# Revit family: Sink-Wall_Mount-KOHLER-Brenham-K-1997
name_source: partatom
category: Plumbing Fixtures
revit_build: Autodesk Revit 2015 (Build: 20140606_1530(x64)
units: mm (PartAtom-declared; Revit-internal decimal feet)

## types (35) — shared parameters
ADA Compliant = Yes
Assembly Code = D2010400
CW Connection = No
Cold Water Inlet = Cold Water Inlet
Date Modified = 08/20/2018
Default Elevation = 34"
Drain Included = No
HW Connection = No
Height = 6 9/16"
Hot Water Inlet = Hot Water Inlet
Length = 21 15/16"
Manufacturer = KOHLER Co.
MasterFormat 1995 = 15410
MasterFormat 2004 = 22.41.16
Material = Vitreous china
Product Documentation Link = http://www.us.kohler.com
Product Name = Brenham
Product Page URL = http://www.us.kohler.com
URL = https://www.us.kohler.com
Vent Connection = No
Waste Connection = Yes
Waste Water Outlet = Waste Water Outlet
Width = 19 3/4"

## per-type parameters (varying)
| type | 1L_SS1L | 1NL_SS1NL | 1NR_SS1NR | 1N_SS1N | 1R_SS1R | 1_SS1 | 4N_SS4N | 4_SS4 | 8N_SS8N | 8_SS8 | Description | Environmental Product Declaration | Finish | Model | Type |
| Antimicrobial Finish, 4" Faucet Holes, 0-White | No | No | No | No | No | No | No | Yes | No | No | Wall-mounted or concealed carrier arm mounted commercial bathroom sink with 4 Inch centerset faucet holes, antimicrobial finish |  | Kohler-Vitreous_China-0-White | K-1997-SS4-0 | 1 |
| Antimicrobial Finish, No Overflow, 4" Faucet Holes,0-White | No | No | No | No | No | No | Yes | No | No | No | Wall-mounted or concealed carrier arm mounted commercial bathroom sink with 4 Inch centerset faucet holes and no overflow, antimicrobial finish |  | Kohler-Vitreous_China-0-White | K-1997-SS4N-0 | 2 |
| Antimicrobial Finish, 8" Faucet Holes,0-White | No | No | No | No | No | No | No | No | No | Yes | Wall-mounted or concealed carrier arm mounted commercial bathroom sink with widespread faucet holes, antimicrobial finish |  | Kohler-Vitreous_China-0-White | K-1997-SS8-0 | 3 |
| Antimicrobial Finish, No Overflow, 8" Faucet Holes, 0-White | No | No | No | No | No | No | No | No | Yes | No | Wall-mounted or concealed carrier arm mounted commercial bathroom sink with widespread faucet holes and no overflow, antimicrobial finish |  | Kohler-Vitreous_China-0-White | K-1997-SS8N-0 | 4 |
| Antimicrobial Finish, No Overflow, Left Soap Dispenser, 1 Faucet Hole, 0-White | No | Yes | No | No | No | No | No | No | No | No | Wall-mounted or concealed carrier arm mounted commercial bathroom sink with single faucet hole, no overflow and left-hand soap dispenser hole, antimicrobial finish |  | Kohler-Vitreous_China-0-White | K-1997-SS1NL-0 | 5 |
| Antimicrobial Finish, Right Soap Dispenser, 1 Faucet Hole, 0-White | No | No | No | No | Yes | No | No | No | No | No | Wall-mounted or concealed carrier arm mounted commercial bathroom sink with single faucet hole and right-hand soap dispenser hole, antimicrobial finish |  | Kohler-Vitreous_China-0-White | K-1997-SS1R-0 | 6 |
| Antimicrobial Finish, No Overflow, 1 Faucet Hole, 0-White | No | No | No | Yes | No | No | No | No | No | No | Wall-mounted or concealed carrier arm mounted commercial bathroom sink with single faucet hole and no overflow, antimicrobial finish |  | Kohler-Vitreous_China-0-White | K-1997-SS1N-0 | 7 |
| Antimicrobial Finish, No Overflow, Right Soap Dispenser, 1 Faucet Hole, 0-White | No | No | Yes | No | No | No | No | No | No | No | Wall-mounted or concealed carrier arm mounted commercial bathroom sink with single faucet hole, no overflow and right-hand soap dispenser hole, antimicrobial finish |  | Kohler-Vitreous_China-0-White | K-1997-SS1NR-0 | 8 |
| Antimicrobial Finish, Left Soap Dispenser, 1 Faucet Hole, 0-White | Yes | No | No | No | No | No | No | No | No | No | Wall-mounted or concealed carrier arm mounted commercial bathroom sink with single faucet hole and left-hand soap dispenser hole, antimicrobial finish |  | Kohler-Vitreous_China-0-White | K-1997-SS1L-0 | 9 |
| Antimicrobial Finish, 1 Faucet Hole, 0-White | No | No | No | No | No | Yes | No | No | No | No | Wall-mounted or concealed carrier arm mounted commercial bathroom sink with single faucet hole, antimicrobial finish |  | Kohler-Vitreous_China-0-White | K-1997-SS1-0 | 10 |
| 4" Faucet Holes, 0-White | No | No | No | No | No | No | No | Yes | No | No | Wall-mounted or concealed carrier arm mounted commercial bathroom sink with 4 Inch center set faucet holes | https://www.us.kohler.com | Kohler-Vitreous_China-0-White | K-1997-4-0 | 11 |
| 4" Faucet Holes, 96-Biscuit | No | No | No | No | No | No | No | Yes | No | No | Wall-mounted or concealed carrier arm mounted commercial bathroom sink with 4 Inch center set faucet holes | https://www.us.kohler.com | Kohler-Vitreous_China-96-Biscuit | K-1997-4-96 | 12 |
| 4" Faucet Holes, 47-Almond | No | No | No | No | No | No | No | Yes | No | No | Wall-mounted or concealed carrier arm mounted commercial bathroom sink with 4 Inch center set faucet holes | https://www.us.kohler.com | Kohler-Vitreous_China-47-Almond | K-1997-4-47 | 13 |
| 4" Faucet Holes, 7-Black Black | No | No | No | No | No | No | No | Yes | No | No | Wall-mounted or concealed carrier arm mounted commercial bathroom sink with 4 Inch center set faucet holes | https://www.us.kohler.com | Kohler-Vitreous_China-7-Black_Black | K-1997-4-7 | 14 |
| No Overflow, 8" Faucet Holes, 0-White | No | No | No | No | No | No | No | No | Yes | No | Wall-mounted or concealed carrier arm mounted commercial bathroom sink with widespread faucet holes and no overflow | https://www.us.kohler.com | Kohler-Vitreous_China-0-White | K-1997-8N-0 | 15 |
| No Overflow, Right Soap Dispenser, 1 Faucet Hole, 0-White | No | No | Yes | No | No | No | No | No | No | No | Wall-mounted or concealed carrier arm mounted commercial bathroom sink with single faucet hole, no overflow and right-hand soap dispenser hole | https://www.us.kohler.com | Kohler-Vitreous_China-0-White | K-1997-1NR-0 | 16 |
| Right Soap Dispenser, 1 Faucet Hole, 0-White | No | No | No | No | Yes | No | No | No | No | No | Wall-mounted or concealed carrier arm mounted commercial bathroom sink with single faucet hole and right-hand soap dispenser hole | https://www.us.kohler.com | Kohler-Vitreous_China-0-White | K-1997-1R-0 | 17 |
| Right Soap Dispenser, 1 Faucet Hole, 96-Biscuit | No | No | No | No | Yes | No | No | No | No | No | Wall-mounted or concealed carrier arm mounted commercial bathroom sink with single faucet hole and right-hand soap dispenser hole | https://www.us.kohler.com | Kohler-Vitreous_China-96-Biscuit | K-1997-1R-96 | 18 |
| Right Soap Dispenser, 1 Faucet Hole, 47-Almond | No | No | No | No | Yes | No | No | No | No | No | Wall-mounted or concealed carrier arm mounted commercial bathroom sink with single faucet hole and right-hand soap dispenser hole | https://www.us.kohler.com | Kohler-Vitreous_China-47-Almond | K-1997-1R-47 | 19 |
| Right Soap Dispenser, 1 Faucet Hole, 7-Black Black | No | No | No | No | Yes | No | No | No | No | No | Wall-mounted or concealed carrier arm mounted commercial bathroom sink with single faucet hole and right-hand soap dispenser hole | https://www.us.kohler.com | Kohler-Vitreous_China-7-Black_Black | K-1997-1R-7 | 20 |
| 8" Faucet Holes, 0-White | No | No | No | No | No | No | No | No | No | Yes | Wall-mounted or concealed carrier arm mounted commercial bathroom sink with widespread faucet holes | https://www.us.kohler.com | Kohler-Vitreous_China-0-White | K-1997-8-0 | 21 |
| 8" Faucet Holes, 96-Biscuit | No | No | No | No | No | No | No | No | No | Yes | Wall-mounted or concealed carrier arm mounted commercial bathroom sink with widespread faucet holes | https://www.us.kohler.com | Kohler-Vitreous_China-96-Biscuit | K-1997-8-96 | 22 |
| 8" Faucet Holes, 47-Almond | No | No | No | No | No | No | No | No | No | Yes | Wall-mounted or concealed carrier arm mounted commercial bathroom sink with widespread faucet holes | https://www.us.kohler.com | Kohler-Vitreous_China-47-Almond | K-1997-8-47 | 23 |
| 8" Faucet Holes, 7-Black Black | No | No | No | No | No | No | No | No | No | Yes | Wall-mounted or concealed carrier arm mounted commercial bathroom sink with widespread faucet holes | https://www.us.kohler.com | Kohler-Vitreous_China-7-Black_Black | K-1997-8-7 | 24 |
| No Overflow, 1 Faucet Hole, 0-White | No | No | No | Yes | No | No | No | No | No | No | Wall-mounted or concealed carrier arm mounted commercial bathroom sink with single faucet hole and no overflow | https://www.us.kohler.com | Kohler-Vitreous_China-0-White | K-1997-1N-0 | 25 |
| No Overflow, Left Soap Dispenser, 1 Faucet Hole, 0-White | No | Yes | No | No | No | No | No | No | No | No | Wall-mounted or concealed carrier arm mounted commercial bathroom sink with single faucet hole, no overflow and left-hand soap dispenser hole | https://www.us.kohler.com | Kohler-Vitreous_China-0-White | K-1997-1NL-0 | 26 |
| 1 Faucet Hole, 0-White | No | No | No | No | No | Yes | No | No | No | No | Wall-mounted or concealed carrier arm mounted commercial bathroom sink with single faucet hole | https://www.us.kohler.com | Kohler-Vitreous_China-0-White | K-1997-1-0 | 27 |
| 1 Faucet Hole, 96-Biscuit | No | No | No | No | No | Yes | No | No | No | No | Wall-mounted or concealed carrier arm mounted commercial bathroom sink with single faucet hole | https://www.us.kohler.com | Kohler-Vitreous_China-96-Biscuit | K-1997-1-96 | 28 |
| 1 Faucet Hole, 47-Almond | No | No | No | No | No | Yes | No | No | No | No | Wall-mounted or concealed carrier arm mounted commercial bathroom sink with single faucet hole | https://www.us.kohler.com | Kohler-Vitreous_China-47-Almond | K-1997-1-47 | 29 |
| 1 Faucet Hole, 7-Black Black | No | No | No | No | No | Yes | No | No | No | No | Wall-mounted or concealed carrier arm mounted commercial bathroom sink with single faucet hole | https://www.us.kohler.com | Kohler-Vitreous_China-7-Black_Black | K-1997-1-7 | 30 |
| No Overflow, 4" Faucet Holes, 0-White | No | No | No | No | No | No | Yes | No | No | No | Wall-mounted or concealed carrier arm mounted commercial bathroom sink with 4 Inch centerset faucet holes and no overflow | https://www.us.kohler.com | Kohler-Vitreous_China-0-White | K-1997-4N-0 | 31 |
| Left Soap Dispenser, 1 Faucet Hole, 0-White | Yes | No | No | No | No | No | No | No | No | No | Wall-mounted or concealed carrier arm mounted commercial bathroom sink with single faucet hole and left-hand soap dispenser hole | https://www.us.kohler.com | Kohler-Vitreous_China-0-White | K-1997-1L-0 | 32 |
| Left Soap Dispenser, 1 Faucet Hole, 96-Biscuit | Yes | No | No | No | No | No | No | No | No | No | Wall-mounted or concealed carrier arm mounted commercial bathroom sink with single faucet hole and left-hand soap dispenser hole | https://www.us.kohler.com | Kohler-Vitreous_China-96-Biscuit | K-1997-1L-96 | 33 |
| Left Soap Dispenser, 1 Faucet Hole, 47-Almond | Yes | No | No | No | No | No | No | No | No | No | Wall-mounted or concealed carrier arm mounted commercial bathroom sink with single faucet hole and left-hand soap dispenser hole | https://www.us.kohler.com | Kohler-Vitreous_China-47-Almond | K-1997-1L-47 | 34 |
| Left Soap Dispenser, 1 Faucet Hole, 7-Black Black | Yes | No | No | No | No | No | No | No | No | No | Wall-mounted or concealed carrier arm mounted commercial bathroom sink with single faucet hole and left-hand soap dispenser hole | https://www.us.kohler.com | Kohler-Vitreous_China-7-Black_Black | K-1997-1L-7 | 35 |

## geometry (parser evidence)
native form markers: Sweep x4
no freeform markers — native parametric forms only
